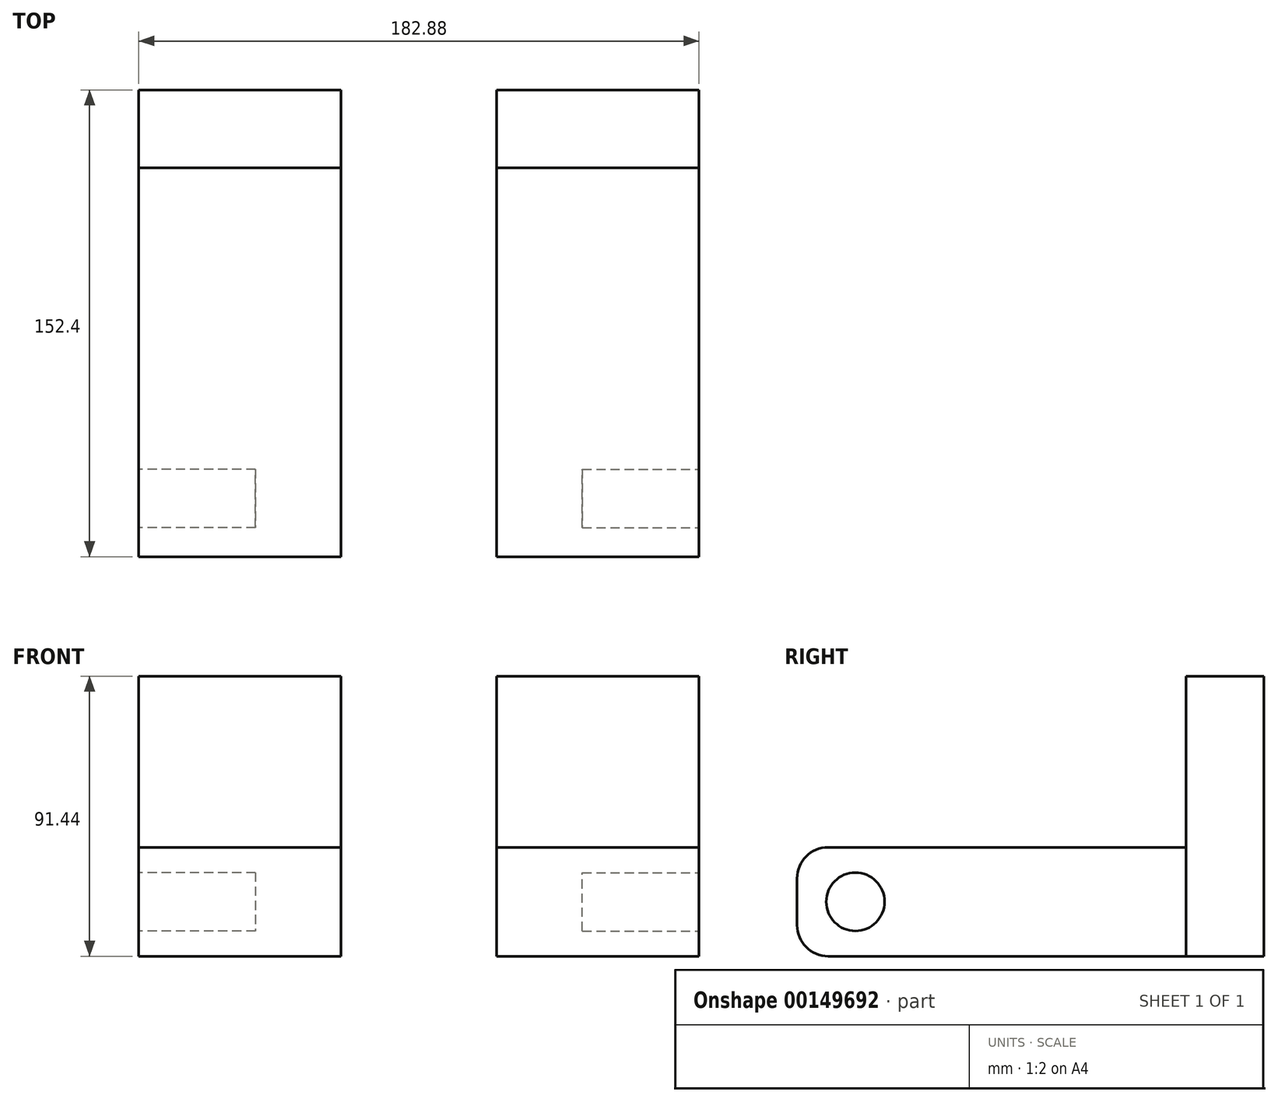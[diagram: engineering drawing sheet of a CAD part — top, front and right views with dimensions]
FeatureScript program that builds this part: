
annotation { "Feature Type Name" : "Feature", "Feature Type Description" : "" }
export const myFeature = defineFeature(function(context is Context, id is Id, definition is map)
    precondition{}
    {
        {
            var Q0;
            Q0=qCreatedBy(makeId("Front.planeOp"),FACE);
            var sketch = newSketch(context, id + "F0", { "sketchPlane" : qUnion([Q0])});
            skLineSegment(sketch, "E0.bottom", {"start": v(-346.76, 150.38) * mm, "end": v(-280.72, 150.38) * mm});
            skLineSegment(sketch, "E0.top", {"start": v(-346.76, 58.94) * mm, "end": v(-280.72, 58.94) * mm});
            skLineSegment(sketch, "E0.left", {"start": v(-346.76, 150.38) * mm, "end": v(-346.76, 58.94) * mm});
            skLineSegment(sketch, "E0.right", {"start": v(-280.72, 150.38) * mm, "end": v(-280.72, 58.94) * mm});
            skLineSegment(sketch, "E1.bottom", {"start": v(-229.92, 150.38) * mm, "end": v(-163.88, 150.38) * mm});
            skLineSegment(sketch, "E1.top", {"start": v(-229.92, 58.94) * mm, "end": v(-163.88, 58.94) * mm});
            skLineSegment(sketch, "E1.left", {"start": v(-229.92, 150.38) * mm, "end": v(-229.92, 58.94) * mm});
            skLineSegment(sketch, "E1.right", {"start": v(-163.88, 150.38) * mm, "end": v(-163.88, 58.94) * mm});
            skLineSegment(sketch, "E2", {"start": v(-280.72, 125.75) * mm, "end": v(-229.92, 125.75) * mm});
            skSolve(sketch);
        }
        {
            var Q0;
            Q0 = qSketchRegion(id + "F0", true);
            extrude(context, id + "F1", {"entities" : qUnion([Q0]), "depth" : 25.4 * mm});
        }
        {
            var Q0;
            Q0=makeQuery(id+"F1.opExtrude","CAP_FACE",FACE,{"disambiguationData":[OSD([sQuery(id+"F0.wireOp",EDGE,"E0.bottom"),sQuery(id+"F0.wireOp",EDGE,"E0.top"),sQuery(id+"F0.wireOp",EDGE,"E0.left"),sQuery(id+"F0.wireOp",EDGE,"E0.right")])],"isStart":false});
            var sketch = newSketch(context, id + "F2", { "sketchPlane" : qUnion([Q0])});
            skLineSegment(sketch, "E3.bottom", {"start": v(-346.76, 94.5) * mm, "end": v(-280.72, 94.5) * mm});
            skLineSegment(sketch, "E3.top", {"start": v(-346.76, 58.94) * mm, "end": v(-280.72, 58.94) * mm});
            skLineSegment(sketch, "E3.left", {"start": v(-346.76, 94.5) * mm, "end": v(-346.76, 58.94) * mm});
            skLineSegment(sketch, "E3.right", {"start": v(-280.72, 94.5) * mm, "end": v(-280.72, 58.94) * mm});
            skLineSegment(sketch, "E4.bottom", {"start": v(-229.92, 94.5) * mm, "end": v(-163.88, 94.5) * mm});
            skLineSegment(sketch, "E4.top", {"start": v(-229.92, 58.94) * mm, "end": v(-163.88, 58.94) * mm});
            skLineSegment(sketch, "E4.left", {"start": v(-229.92, 94.5) * mm, "end": v(-229.92, 58.94) * mm});
            skLineSegment(sketch, "E4.right", {"start": v(-163.88, 94.5) * mm, "end": v(-163.88, 58.94) * mm});
            skLineSegment(sketch, "E5", {"start": v(-280.72, 72.5) * mm, "end": v(-229.92, 72.5) * mm});
            skSolve(sketch);
        }
        {
            var Q0;
            Q0 = qSketchRegion(id + "F2", true);
            extrude(context, id + "F3", {"entities" : qUnion([Q0]), "depth" : 127 * mm});
        }
        {
            var Q0;
            Q0=makeQuery(id+"F3.opExtrude","SWEPT_FACE",FACE,{"disambiguationData":[OSD([sQuery(id+"F2.wireOp",EDGE,"E4.right")])]});
            var sketch = newSketch(context, id + "F4", { "sketchPlane" : qUnion([Q0])});
            skCircle(sketch, "E6", {"center": v(-133.35, 76.72) * mm, "radius": 9.53 * mm});
            skPoint(sketch, "E6.centerSnap0", {"position": v(-152.4, 76.72) * mm});
            skSolve(sketch);
        }
        {
            var Q0;
            Q0=makeQuery(id+"F4.imprint","IMPRINT",FACE,{"disambiguationData":[TD([[makeQuery(id+"F4.imprint","IMPRINT",EDGE,{"derivedFrom":sQuery(id+"F4.wireOp",EDGE,"E6")}),1.0]])]});
            extrude(context, id + "F5", {"entities" : qUnion([Q0]), "operationType" : NewBodyOperationType.REMOVE, "oppositeDirection" : true, "depth" : 38.1 * mm});
        }
        {
            var Q0;
            Q0=makeQuery(id+"F3.opExtrude","SWEPT_FACE",FACE,{"disambiguationData":[OSD([sQuery(id+"F2.wireOp",EDGE,"E3.left")])]});
            var sketch = newSketch(context, id + "F6", { "sketchPlane" : qUnion([Q0])});
            skCircle(sketch, "E7", {"center": v(133.35, 76.72) * mm, "radius": 9.53 * mm});
            skPoint(sketch, "E7.centerSnap0", {"position": v(152.4, 76.72) * mm});
            skSolve(sketch);
        }
        {
            var Q0;
            Q0=makeQuery(id+"F6.imprint","IMPRINT",FACE,{"disambiguationData":[TD([[makeQuery(id+"F6.imprint","IMPRINT",EDGE,{"derivedFrom":sQuery(id+"F6.wireOp",EDGE,"E7")}),1.0]])]});
            extrude(context, id + "F7", {"entities" : qUnion([Q0]), "operationType" : NewBodyOperationType.REMOVE, "oppositeDirection" : true, "depth" : 38.1 * mm});
        }
        {
            var Q0;
            Q0=makeQuery(id+"F3.opExtrude","CAP_EDGE",EDGE,{"disambiguationData":[OSD([sQuery(id+"F2.wireOp",EDGE,"E3.bottom")])],"isStart":false});
            var Q1;
            Q1=makeQuery(id+"F3.opExtrude","CAP_EDGE",EDGE,{"disambiguationData":[OSD([sQuery(id+"F2.wireOp",EDGE,"E3.top")])],"isStart":false});
            fillet(context, id + "F8", {"entities" : qUnion([Q0, Q1]), "radius" : 10.16 * mm, "tangentPropagation" : true, "allowEdgeOverflow" : false});
        }
        {
            var Q0;
            Q0=makeQuery(id+"F3.opExtrude","CAP_EDGE",EDGE,{"disambiguationData":[OSD([sQuery(id+"F2.wireOp",EDGE,"E4.top")])],"isStart":false});
            var Q1;
            Q1=makeQuery(id+"F3.opExtrude","CAP_EDGE",EDGE,{"disambiguationData":[OSD([sQuery(id+"F2.wireOp",EDGE,"E4.bottom")])],"isStart":false});
            fillet(context, id + "F9", {"entities" : qUnion([Q0, Q1]), "radius" : 10.16 * mm, "tangentPropagation" : true, "allowEdgeOverflow" : false});
        }
    });
